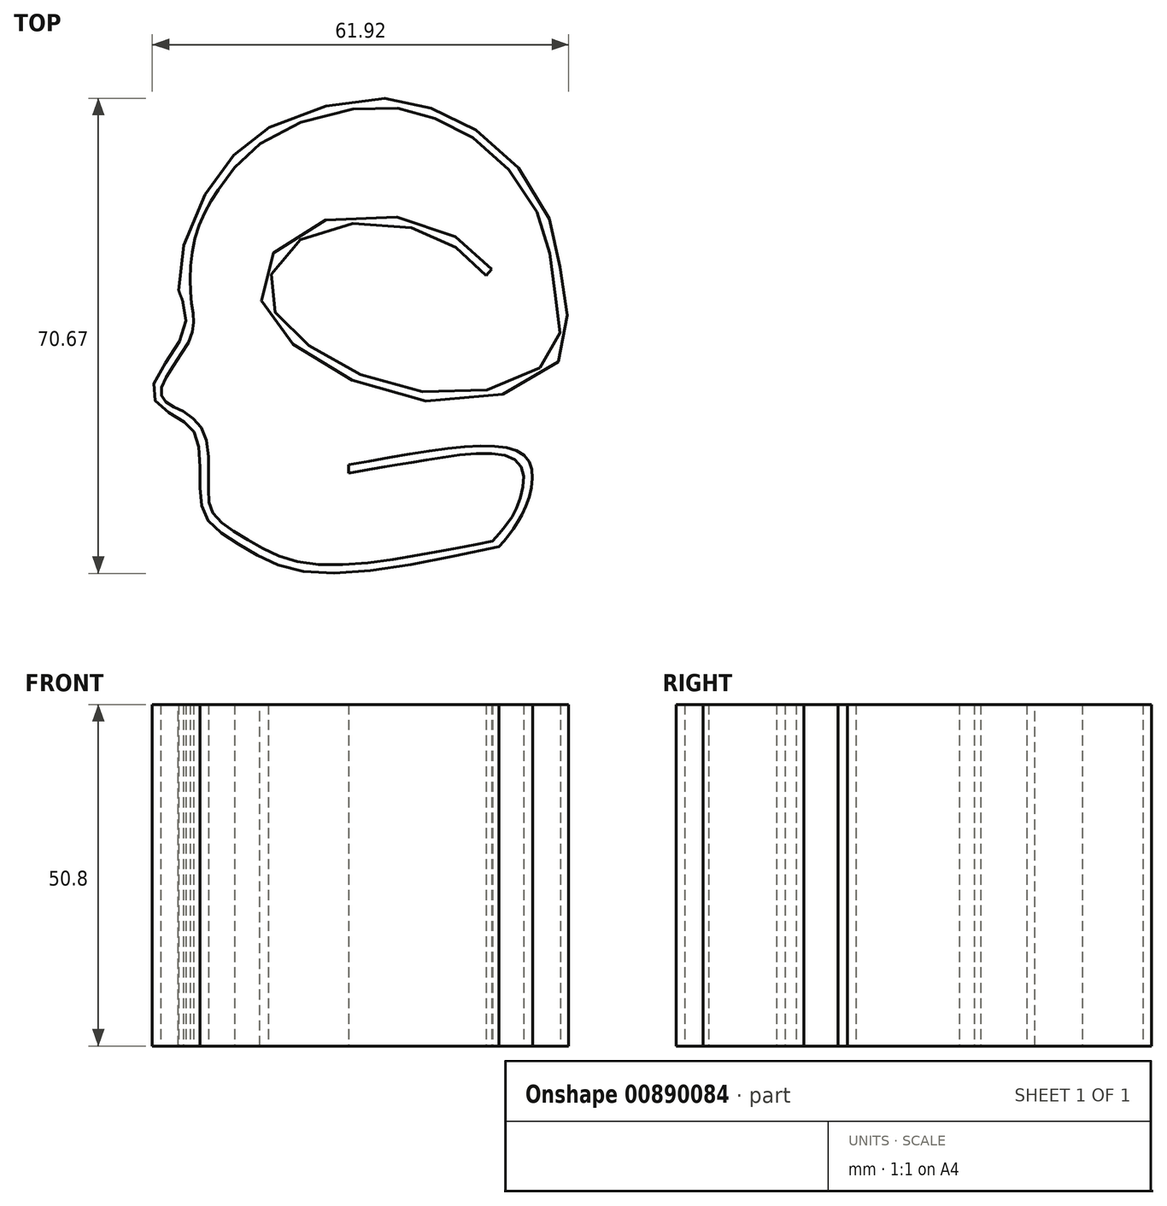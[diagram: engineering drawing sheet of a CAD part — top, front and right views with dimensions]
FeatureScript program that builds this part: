
annotation { "Feature Type Name" : "Feature", "Feature Type Description" : "" }
export const myFeature = defineFeature(function(context is Context, id is Id, definition is map)
    precondition{}
    {
        {
            var Q0;
            Q0=qCreatedBy(makeId("Top.planeOp"),FACE);
            var sketch = newSketch(context, id + "F0", { "sketchPlane" : qUnion([Q0])});
            skPoint(sketch, "E0.first.point", {"position": v(-28.58, 9.52) * mm});
            skPoint(sketch, "E0.third.point", {"position": v(28.57, 9.53) * mm});
            skFitSpline(sketch, "E1", {"points": [v(-28.58, 9.52) * mm, v(-27.87, 3.2) * mm, v(-32.5, -5.6) * mm, v(-28.57, -9.53) * mm, v(-25.98, -12.12) * mm, v(-25.4, -19.05) * mm, v(-24.41, -24.41) * mm, v(-19.05, -28.58) * mm, v(-9.53, -32.34) * mm, v(19.05, -28.58) * mm], "startDerivative": vector(24.88, -61.7) * mm, "endDerivative": vector(157.94, 33.81) * mm});
            skFitSpline(sketch, "E2", {"points": [v(-27.77, 7.54) * mm, v(-28.58, 9.52) * mm, v(-26.94, 19.05) * mm, v(-21.3, 28.58) * mm, v(-14.87, 33.92) * mm, v(0, 38.1) * mm, v(9.52, 36.47) * mm, v(19.05, 30.82) * mm, v(26.94, 19.05) * mm, v(28.58, 9.53) * mm, v(28.58, 0) * mm, v(11.97, -7.08) * mm, v(-9.52, 0) * mm, v(-16.5, 9.53) * mm, v(-9.52, 19.05) * mm, v(9.52, 19.05) * mm, v(17.97, 12.72) * mm], "startDerivative": vector(-37.34, 57.92) * mm, "endDerivative": vector(114.1, -120.75) * mm});
            skFitSpline(sketch, "E3", {"points": [v(19.05, -28.58) * mm, v(22.9, -22.9) * mm, v(22.98, -15.12) * mm, v(-3.31, -16.37) * mm], "startDerivative": vector(16.9, 19.82) * mm, "endDerivative": vector(-71.14, -12.24) * mm});
            skLineSegment(sketch, "E4", {"start": v(-3.31, -16.37) * mm, "end": v(-3.31, -17.64) * mm});
            skLineSegment(sketch, "E5", {"start": v(17.97, 12.72) * mm, "end": v(17.15, 11.75) * mm});
            skFitSpline(sketch, "E6", {"points": [v(-3.31, -17.64) * mm, v(8.23, -15.66) * mm, v(21.9, -16.02) * mm, v(21.63, -22.9) * mm, v(19.37, -26.27) * mm, v(18.08, -27.76) * mm], "startDerivative": vector(39.54, 7.02) * mm, "endDerivative": vector(-11.4, -13.16) * mm});
            skFitSpline(sketch, "E7", {"points": [v(18.08, -27.76) * mm, v(7.92, -29.66) * mm, v(-9.4, -31.07) * mm, v(-18.48, -27.44) * mm, v(-23.45, -23.58) * mm, v(-24.13, -19.05) * mm, v(-24.87, -11.5) * mm, v(-27.9, -8.45) * mm], "startDerivative": vector(-56.8, -10.98) * mm, "endDerivative": vector(-34.26, 22.78) * mm});
            skFitSpline(sketch, "E8", {"points": [v(-27.9, -8.45) * mm, v(-31.23, -5.6) * mm, v(-26.82, 2.48) * mm, v(-26.72, 8.2) * mm, v(-25.8, 18.5) * mm, v(-20.28, 27.81) * mm], "startDerivative": vector(-33.16, 14.56) * mm, "endDerivative": vector(27.9, 37.15) * mm});
            skFitSpline(sketch, "E9", {"points": [v(-20.28, 27.81) * mm, v(-14.26, 32.81) * mm, v(0, 36.83) * mm, v(8.99, 35.32) * mm, v(18.2, 29.88) * mm, v(25.84, 18.43) * mm, v(27.3, 9.53) * mm, v(27.44, 0.56) * mm, v(11.97, -5.8) * mm, v(-8.67, 0.94) * mm, v(-15.23, 9.53) * mm, v(-9.02, 17.88) * mm, v(8.72, 18.07) * mm, v(17.15, 11.75) * mm], "startDerivative": vector(79.26, 84.65) * mm, "endDerivative": vector(95.97, -101.63) * mm});
            skSolve(sketch);
        }
        {
            var Q0;
            Q0=makeQuery(id+"F0.imprint","IMPRINT",FACE,{"disambiguationData":[TD([[makeQuery(id+"F0.imprint","IMPRINT",EDGE,{"derivedFrom":sQuery(id+"F0.wireOp",EDGE,"E1")}),1.0]])]});
            extrude(context, id + "F1", {"entities" : qUnion([Q0]), "depth" : 50.8 * mm, "offsetDistance" : 25.4 * mm});
        }
    });
